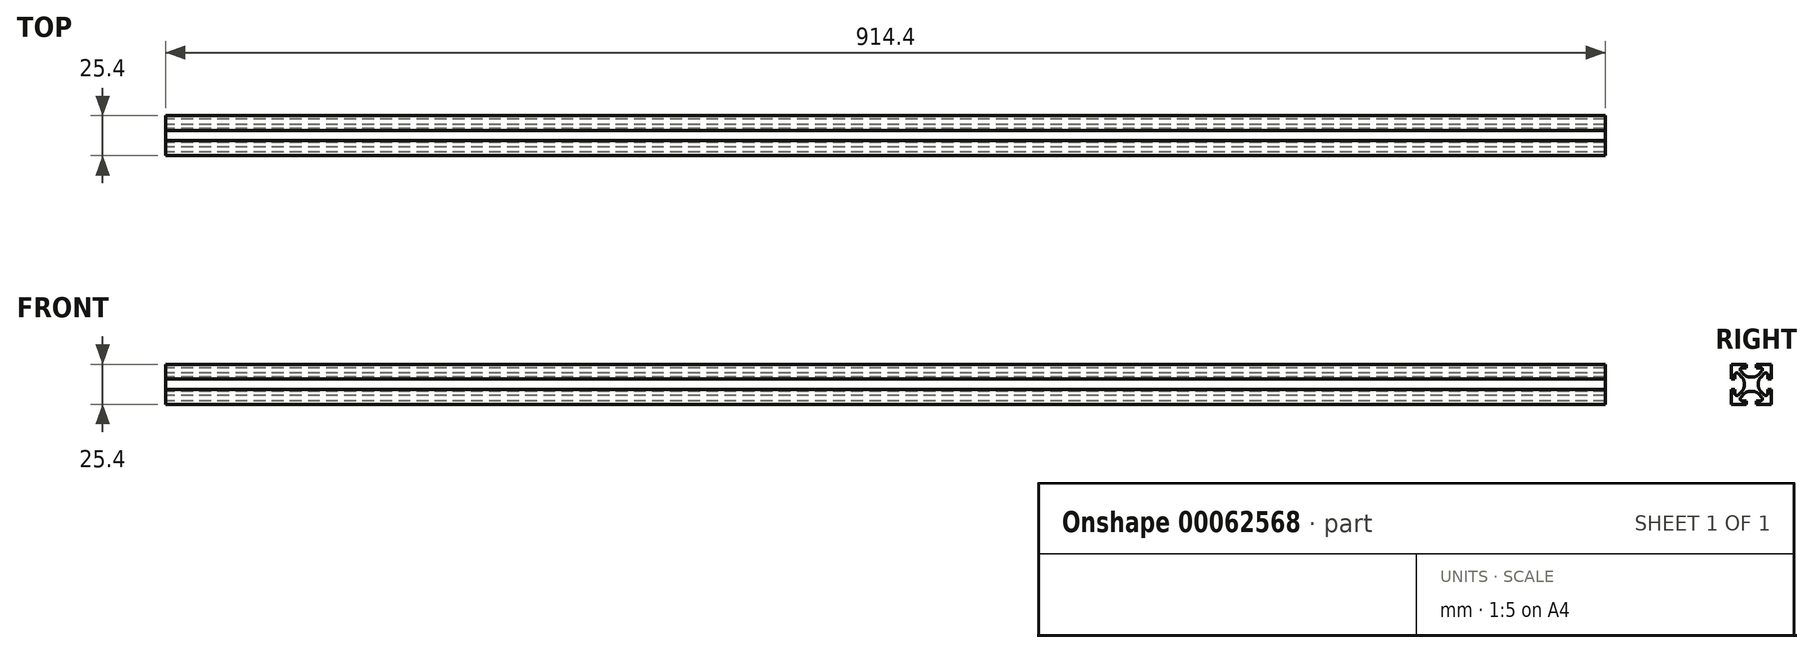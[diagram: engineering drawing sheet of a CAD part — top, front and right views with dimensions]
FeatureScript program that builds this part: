
annotation { "Feature Type Name" : "Feature", "Feature Type Description" : "" }
export const myFeature = defineFeature(function(context is Context, id is Id, definition is map)
    precondition{}
    {
        {
            var Q0;
            Q0=qCreatedBy(makeId("Right.planeOp"),FACE);
            var sketch = newSketch(context, id + "F0", { "sketchPlane" : qUnion([Q0])});
            skLineSegment(sketch, "E0.bottom", {"start": v(0, 0) * mm, "end": v(4.5, 0) * mm, "construction": true});
            skLineSegment(sketch, "E0.top", {"start": v(0, 12.7) * mm, "end": v(3.24, 12.7) * mm});
            skLineSegment(sketch, "E0.left", {"start": v(0, 0) * mm, "end": v(0, 4.5) * mm, "construction": true});
            skLineSegment(sketch, "E0.right", {"start": v(12.7, 0) * mm, "end": v(12.7, 3.24) * mm});
            skLineSegment(sketch, "E1", {"start": v(12.7, 3.24) * mm, "end": v(12.7, 12.7) * mm});
            skLineSegment(sketch, "E2", {"start": v(3.24, 12.7) * mm, "end": v(12.7, 12.7) * mm});
            skLineSegment(sketch, "E3", {"start": v(0, 0) * mm, "end": v(10.5, 10.5) * mm, "construction": true});
            skLineSegment(sketch, "E4", {"start": v(0, 4.5) * mm, "end": v(0, 12.7) * mm, "construction": true});
            skLineSegment(sketch, "E5", {"start": v(4.5, 0) * mm, "end": v(12.7, 0) * mm, "construction": true});
            skLineSegment(sketch, "E6.0", {"start": v(6, 4.43) * mm, "end": v(8.32, 6.76) * mm});
            skLineSegment(sketch, "E7.0", {"start": v(4.43, 6) * mm, "end": v(6.76, 8.32) * mm});
            skLineSegment(sketch, "E8.top", {"start": v(3.24, 10.5) * mm, "end": v(5.86, 10.5) * mm});
            skLineSegment(sketch, "E8.left", {"start": v(3.24, 12.7) * mm, "end": v(3.24, 10.5) * mm});
            skLineSegment(sketch, "E8.right", {"start": v(12.7, 12.7) * mm, "end": v(12.7, 10.5) * mm});
            skLineSegment(sketch, "E9.bottom", {"start": v(12.7, 3.24) * mm, "end": v(10.5, 3.24) * mm});
            skLineSegment(sketch, "E9.top", {"start": v(12.7, 12.7) * mm, "end": v(10.5, 12.7) * mm});
            skLineSegment(sketch, "E9.right", {"start": v(10.5, 3.24) * mm, "end": v(10.5, 5.86) * mm});
            skLineSegment(sketch, "E10", {"start": v(0, 4.5) * mm, "end": v(0.84, 4.5) * mm});
            skLineSegment(sketch, "E11", {"start": v(4.5, 0) * mm, "end": v(4.5, 0.84) * mm});
            skArc(sketch, "E12.filletArc", {"start": v(0.84, 4.5) * mm, "mid": v(2.79, 4.9) * mm, "end": v(4.43, 6) * mm});
            skArc(sketch, "E13.filletArc", {"start": v(6, 4.43) * mm, "mid": v(4.9, 2.79) * mm, "end": v(4.5, 0.84) * mm});
            skArc(sketch, "E14.filletArc", {"start": v(6.76, 8.32) * mm, "mid": v(7.03, 9.7) * mm, "end": v(5.86, 10.5) * mm});
            skArc(sketch, "E15.filletArc", {"start": v(10.5, 5.86) * mm, "mid": v(9.7, 7.03) * mm, "end": v(8.32, 6.76) * mm});
            skArc(sketch, "E16.1.0", {"start": v(-4.43, 6) * mm, "mid": v(-2.79, 4.9) * mm, "end": v(-0.84, 4.5) * mm});
            skLineSegment(sketch, "E16.1.1", {"start": v(-3.24, 10.5) * mm, "end": v(-5.86, 10.5) * mm});
            skLineSegment(sketch, "E16.1.2", {"start": v(-3.24, 12.7) * mm, "end": v(-12.7, 12.7) * mm});
            skLineSegment(sketch, "E16.1.4", {"start": v(-4.5, 0) * mm, "end": v(-12.7, 0) * mm, "construction": true});
            skLineSegment(sketch, "E16.1.5", {"start": v(0, 12.7) * mm, "end": v(-3.24, 12.7) * mm});
            skLineSegment(sketch, "E16.1.6", {"start": v(-12.7, 0) * mm, "end": v(-12.7, 3.24) * mm});
            skLineSegment(sketch, "E16.1.7", {"start": v(-12.7, 3.24) * mm, "end": v(-10.5, 3.24) * mm});
            skLineSegment(sketch, "E16.1.8", {"start": v(0, 0) * mm, "end": v(-4.5, 0) * mm, "construction": true});
            skArc(sketch, "E16.1.9", {"start": v(-8.32, 6.76) * mm, "mid": v(-9.7, 7.03) * mm, "end": v(-10.5, 5.86) * mm});
            skLineSegment(sketch, "E16.1.10", {"start": v(0, 0) * mm, "end": v(-10.5, 10.5) * mm, "construction": true});
            skLineSegment(sketch, "E16.1.12", {"start": v(-6, 4.43) * mm, "end": v(-8.32, 6.76) * mm});
            skLineSegment(sketch, "E16.1.13", {"start": v(-12.7, 3.24) * mm, "end": v(-12.7, 12.7) * mm});
            skLineSegment(sketch, "E16.1.14", {"start": v(-10.5, 3.24) * mm, "end": v(-10.5, 5.86) * mm});
            skLineSegment(sketch, "E16.1.15", {"start": v(-3.24, 12.7) * mm, "end": v(-3.24, 10.5) * mm});
            skArc(sketch, "E16.1.16", {"start": v(-4.5, 0.84) * mm, "mid": v(-4.9, 2.79) * mm, "end": v(-6, 4.43) * mm});
            skArc(sketch, "E16.1.17", {"start": v(-5.86, 10.5) * mm, "mid": v(-7.03, 9.7) * mm, "end": v(-6.76, 8.32) * mm});
            skLineSegment(sketch, "E16.1.18", {"start": v(-12.7, 12.7) * mm, "end": v(-12.7, 10.5) * mm});
            skLineSegment(sketch, "E16.1.19", {"start": v(-3.24, 12.7) * mm, "end": v(-12.7, 12.7) * mm});
            skLineSegment(sketch, "E16.1.20", {"start": v(-4.43, 6) * mm, "end": v(-6.76, 8.32) * mm});
            skLineSegment(sketch, "E16.1.21", {"start": v(-12.7, 3.24) * mm, "end": v(-12.7, 12.7) * mm});
            skLineSegment(sketch, "E16.1.22", {"start": v(-12.7, 12.7) * mm, "end": v(-10.5, 12.7) * mm});
            skLineSegment(sketch, "E16.1.23", {"start": v(0, 4.5) * mm, "end": v(-0.84, 4.5) * mm});
            skLineSegment(sketch, "E16.1.24", {"start": v(-4.5, 0) * mm, "end": v(-4.5, 0.84) * mm});
            skArc(sketch, "E16.2.0", {"start": v(-6, -4.43) * mm, "mid": v(-4.9, -2.79) * mm, "end": v(-4.5, -0.84) * mm});
            skLineSegment(sketch, "E16.2.1", {"start": v(-10.5, -3.24) * mm, "end": v(-10.5, -5.86) * mm});
            skLineSegment(sketch, "E16.2.2", {"start": v(-12.7, -3.24) * mm, "end": v(-12.7, -12.7) * mm});
            skLineSegment(sketch, "E16.2.3", {"start": v(0, 0) * mm, "end": v(-4.5, 0) * mm, "construction": true});
            skLineSegment(sketch, "E16.2.4", {"start": v(0, -4.5) * mm, "end": v(0, -12.7) * mm, "construction": true});
            skLineSegment(sketch, "E16.2.5", {"start": v(-12.7, 0) * mm, "end": v(-12.7, -3.24) * mm});
            skLineSegment(sketch, "E16.2.6", {"start": v(0, -12.7) * mm, "end": v(-3.24, -12.7) * mm});
            skLineSegment(sketch, "E16.2.7", {"start": v(-3.24, -12.7) * mm, "end": v(-3.24, -10.5) * mm});
            skLineSegment(sketch, "E16.2.8", {"start": v(0, 0) * mm, "end": v(0, -4.5) * mm, "construction": true});
            skArc(sketch, "E16.2.9", {"start": v(-6.76, -8.32) * mm, "mid": v(-7.03, -9.7) * mm, "end": v(-5.86, -10.5) * mm});
            skLineSegment(sketch, "E16.2.10", {"start": v(0, 0) * mm, "end": v(-10.5, -10.5) * mm, "construction": true});
            skLineSegment(sketch, "E16.2.11", {"start": v(-4.5, 0) * mm, "end": v(-12.7, 0) * mm, "construction": true});
            skLineSegment(sketch, "E16.2.12", {"start": v(-4.43, -6) * mm, "end": v(-6.76, -8.32) * mm});
            skLineSegment(sketch, "E16.2.13", {"start": v(-3.24, -12.7) * mm, "end": v(-12.7, -12.7) * mm});
            skLineSegment(sketch, "E16.2.14", {"start": v(-3.24, -10.5) * mm, "end": v(-5.86, -10.5) * mm});
            skLineSegment(sketch, "E16.2.15", {"start": v(-12.7, -3.24) * mm, "end": v(-10.5, -3.24) * mm});
            skArc(sketch, "E16.2.16", {"start": v(-0.84, -4.5) * mm, "mid": v(-2.79, -4.9) * mm, "end": v(-4.43, -6) * mm});
            skArc(sketch, "E16.2.17", {"start": v(-10.5, -5.86) * mm, "mid": v(-9.7, -7.03) * mm, "end": v(-8.32, -6.76) * mm});
            skLineSegment(sketch, "E16.2.18", {"start": v(-12.7, -12.7) * mm, "end": v(-10.5, -12.7) * mm});
            skLineSegment(sketch, "E16.2.19", {"start": v(-12.7, -3.24) * mm, "end": v(-12.7, -12.7) * mm});
            skLineSegment(sketch, "E16.2.20", {"start": v(-6, -4.43) * mm, "end": v(-8.32, -6.76) * mm});
            skLineSegment(sketch, "E16.2.21", {"start": v(-3.24, -12.7) * mm, "end": v(-12.7, -12.7) * mm});
            skLineSegment(sketch, "E16.2.22", {"start": v(-12.7, -12.7) * mm, "end": v(-12.7, -10.5) * mm});
            skLineSegment(sketch, "E16.2.23", {"start": v(-4.5, 0) * mm, "end": v(-4.5, -0.84) * mm});
            skLineSegment(sketch, "E16.2.24", {"start": v(0, -4.5) * mm, "end": v(-0.84, -4.5) * mm});
            skArc(sketch, "E16.3.0", {"start": v(4.43, -6) * mm, "mid": v(2.79, -4.9) * mm, "end": v(0.84, -4.5) * mm});
            skLineSegment(sketch, "E16.3.1", {"start": v(3.24, -10.5) * mm, "end": v(5.86, -10.5) * mm});
            skLineSegment(sketch, "E16.3.2", {"start": v(3.24, -12.7) * mm, "end": v(12.7, -12.7) * mm});
            skLineSegment(sketch, "E16.3.3", {"start": v(0, 0) * mm, "end": v(0, -4.5) * mm, "construction": true});
            skLineSegment(sketch, "E16.3.5", {"start": v(0, -12.7) * mm, "end": v(3.24, -12.7) * mm});
            skLineSegment(sketch, "E16.3.6", {"start": v(12.7, 0) * mm, "end": v(12.7, -3.24) * mm});
            skLineSegment(sketch, "E16.3.7", {"start": v(12.7, -3.24) * mm, "end": v(10.5, -3.24) * mm});
            skArc(sketch, "E16.3.9", {"start": v(8.32, -6.76) * mm, "mid": v(9.7, -7.03) * mm, "end": v(10.5, -5.86) * mm});
            skLineSegment(sketch, "E16.3.10", {"start": v(0, 0) * mm, "end": v(10.5, -10.5) * mm, "construction": true});
            skLineSegment(sketch, "E16.3.11", {"start": v(0, -4.5) * mm, "end": v(0, -12.7) * mm, "construction": true});
            skLineSegment(sketch, "E16.3.12", {"start": v(6, -4.43) * mm, "end": v(8.32, -6.76) * mm});
            skLineSegment(sketch, "E16.3.13", {"start": v(12.7, -3.24) * mm, "end": v(12.7, -12.7) * mm});
            skLineSegment(sketch, "E16.3.14", {"start": v(10.5, -3.24) * mm, "end": v(10.5, -5.86) * mm});
            skLineSegment(sketch, "E16.3.15", {"start": v(3.24, -12.7) * mm, "end": v(3.24, -10.5) * mm});
            skArc(sketch, "E16.3.16", {"start": v(4.5, -0.84) * mm, "mid": v(4.9, -2.79) * mm, "end": v(6, -4.43) * mm});
            skArc(sketch, "E16.3.17", {"start": v(5.86, -10.5) * mm, "mid": v(7.03, -9.7) * mm, "end": v(6.76, -8.32) * mm});
            skLineSegment(sketch, "E16.3.18", {"start": v(12.7, -12.7) * mm, "end": v(12.7, -10.5) * mm});
            skLineSegment(sketch, "E16.3.19", {"start": v(3.24, -12.7) * mm, "end": v(12.7, -12.7) * mm});
            skLineSegment(sketch, "E16.3.20", {"start": v(4.43, -6) * mm, "end": v(6.76, -8.32) * mm});
            skLineSegment(sketch, "E16.3.21", {"start": v(12.7, -3.24) * mm, "end": v(12.7, -12.7) * mm});
            skLineSegment(sketch, "E16.3.22", {"start": v(12.7, -12.7) * mm, "end": v(10.5, -12.7) * mm});
            skLineSegment(sketch, "E16.3.23", {"start": v(0, -4.5) * mm, "end": v(0.84, -4.5) * mm});
            skLineSegment(sketch, "E16.3.24", {"start": v(4.5, 0) * mm, "end": v(4.5, -0.84) * mm});
            skPoint(sketch, "E16.center", {"position": v(0, 0) * mm});
            skSolve(sketch);
        }
        {
            var Q0;
            Q0=makeQuery(id+"F0.imprint","IMPRINT",FACE,{"disambiguationData":[TD([[makeQuery(id+"F0.imprint","IMPRINT",EDGE,{"derivedFrom":sQuery(id+"F0.wireOp",EDGE,"E6.0")}),1.0]])]});
            extrude(context, id + "F1", {"entities" : qUnion([Q0]), "depth" : 914.4 * mm});
        }
    });
